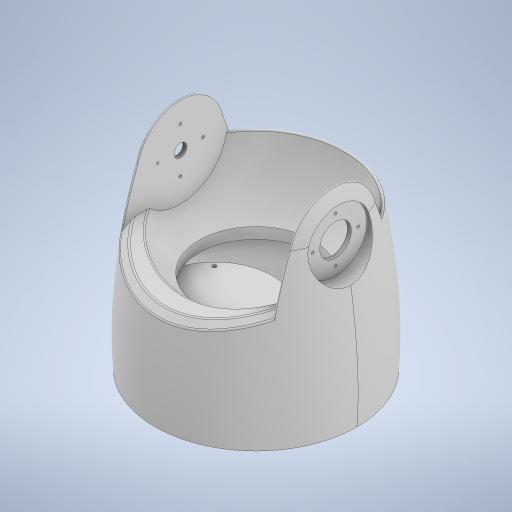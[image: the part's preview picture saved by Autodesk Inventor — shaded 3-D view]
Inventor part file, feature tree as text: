
AUTODESK INVENTOR PART (.ipt)
format: ipt  version: 2023.1 (Build 271208000, 208)  size: 813,568 bytes
history: native  units: mm
features: sketch x15, extrude x14, fillet x4, other x3, revolve x3, chamfer x3, mirror x2, projected_geometry x2, pattern_circular x1
ambient origin geometry x8: Origin, YZ Plane, XZ Plane, XY Plane, X Axis, Y Axis, Z Axis, Center Point
bodies: Body1 (feature_tree)
feature tree (47):
  other  "솔리드1"
  revolve  "회전1"
  sketch  "스케치2"
  revolve  "회전2"
  revolve  "회전3"
  extrude  "돌출3"  Depth=120.0mm
  extrude  "돌출4"  Depth=140.0mm
  chamfer  "모따기1"  Distance=60.0mm
  fillet  "모깎기1"  Radius=130.0mm
  extrude  "돌출5"  Depth=160.0mm
  fillet  "모깎기2"  [1 undecoded]
  fillet  "모깎기3"  Radius=120.0mm
  extrude  "돌출6"  Depth=141.0mm
  other  "작업 평면2"
  extrude  "돌출7"  TaperAngle=90.0deg  [1 undecoded]
  mirror  "미러1"
  extrude  "돌출9"  Depth=4.0mm
  extrude  "돌출10"  TaperAngle=90.0deg  [1 undecoded]
  mirror  "미러2"
  sketch  "스케치13"
  extrude  "돌출11"  Depth=10.0mm
  extrude  "돌출12"  Depth=371.75mm TaperAngle=0.0deg
  sketch  "스케치15"
  extrude  "돌출13"  Depth=25.0mm
  extrude  "돌출14"  Depth=140.0mm
  pattern_circular  "원형 패턴1"  [2 undecoded]
  extrude  "돌출15"  Depth=103.5mm TaperAngle=0.0deg
  fillet  "모깎기4"  Radius=5.0mm
  other  "작업 평면4"
  extrude  "돌출16"  Depth=2.0mm
  chamfer  "모따기2"  Distance=90.0mm
  extrude  "돌출17"  Depth=103.5mm TaperAngle=0.0deg
  chamfer  "모따기3"  Distance=1.0mm
  sketch  "스케치1"
  sketch  "스케치3"
  projected_geometry  "투영된 루프1"
  sketch  "스케치5"
  sketch  "스케치6"
  sketch  "스케치7"
  sketch  "스케치8"
  projected_geometry  "투영된 루프2"
  sketch  "스케치9"
  sketch  "스케치11"
  sketch  "스케치12"
  sketch  "스케치16"
  sketch  "스케치17"
  sketch  "스케치18"
note: 5 required parameter values undecoded (feature->parameter linkage not recoverable at this tier; creation-order binding heuristic only, values carry confidence <= 0.55)
